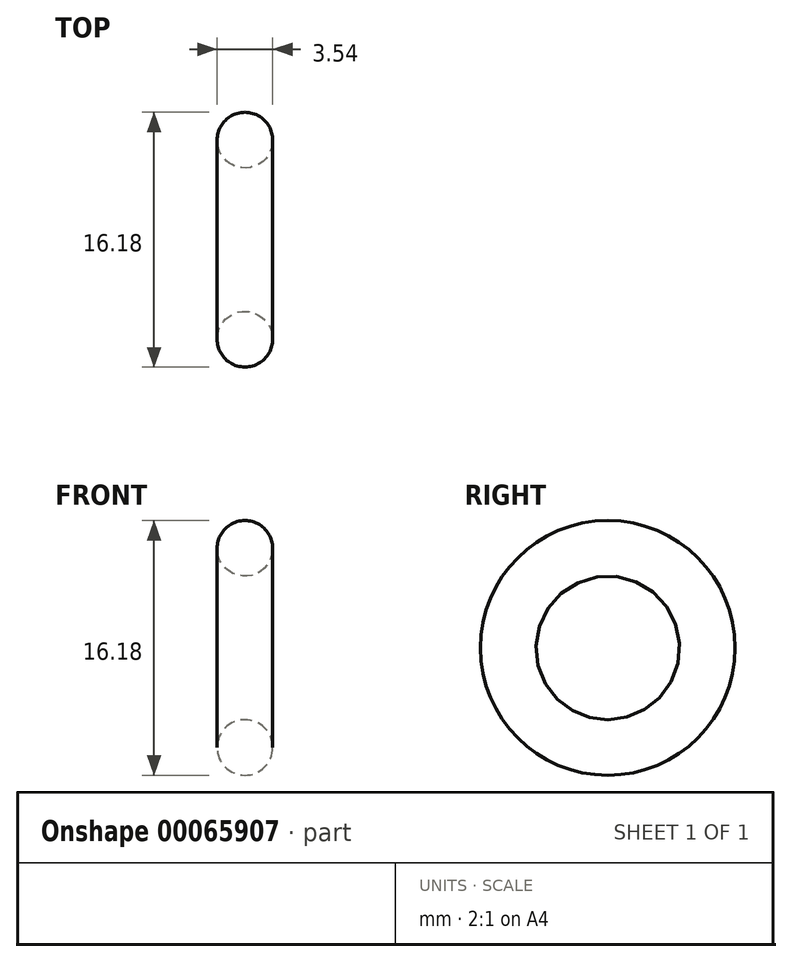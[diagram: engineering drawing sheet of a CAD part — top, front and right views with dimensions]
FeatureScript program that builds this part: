
annotation { "Feature Type Name" : "Feature", "Feature Type Description" : "" }
export const myFeature = defineFeature(function(context is Context, id is Id, definition is map)
    precondition{}
    {
        {
            var Q0;
            Q0=qCreatedBy(makeId("Front.planeOp"),FACE);
            var sketch = newSketch(context, id + "F0", { "sketchPlane" : qUnion([Q0])});
            skLineSegment(sketch, "E0", {"start": v(0, 0) * mm, "end": v(-6.06, 0) * mm, "construction": true});
            skCircle(sketch, "E1", {"center": v(0, 6.32) * mm, "radius": 1.77 * mm});
            skSolve(sketch);
        }
        {
            var Q0;
            Q0=makeQuery(id+"F0.imprint","IMPRINT",FACE,{"disambiguationData":[TD([[makeQuery(id+"F0.imprint","IMPRINT",EDGE,{"derivedFrom":sQuery(id+"F0.wireOp",EDGE,"E1")}),1.0]])]});
            var Q1;
            Q1=sQuery(id+"F0.wireOp",EDGE,"E0");
            revolve(context, id + "F1", {"entities" : qUnion([Q0]), "axis" : qUnion([Q1]), "revolveType" : RevolveType.FULL});
        }
    });
